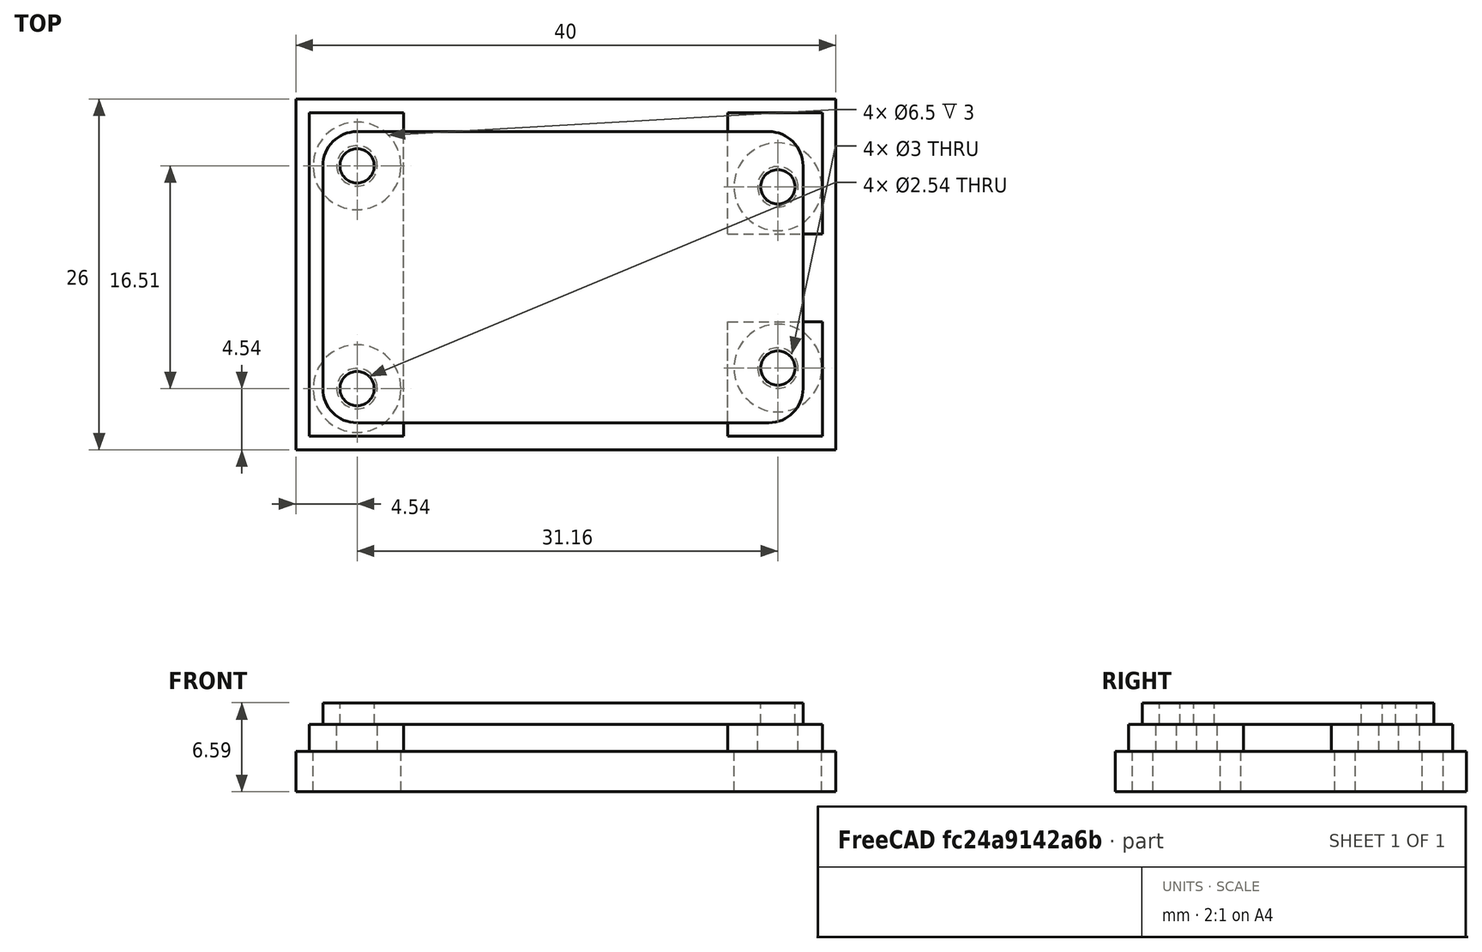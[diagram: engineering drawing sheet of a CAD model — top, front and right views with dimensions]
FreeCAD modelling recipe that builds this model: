
FCSTD DOCUMENT  (FreeCAD 0.19R)
Label: PowerRegulatorBase
License: All rights reserved
LicenseURL: http://en.wikipedia.org/wiki/All_rights_reserved
objects: Part::Cylinder×12, Part::MultiFuse×6, Part::Box×5, Part::Cut×2, Part::Fillet×1
note: 26 computed .brp shape members not serialized (recipe doc carries the construction recipe); baked Part::Feature solids carry a one-line shape summary decoded from their .brp

FEATURE [Part::Box] Box  label="Cube"
  AttacherType = Attacher::AttachEngine3D
  Height = 1.5875
  Length = 35.56
  Width = 21.59
FEATURE [Part::Fillet] Fillet
  Base = -> Box
  Edges = 4 edges r=2.54: [Edge1,Edge3,Edge5,Edge7]
FEATURE [Part::Cylinder] Cylinder
  Angle = 360
  AttacherType = Attacher::AttachEngine3D
  Height = 1.6
  Placement = pos=(2.54,2.54,0) rot=(0,0,1;0rad)
  Radius = 1.27
FEATURE [Part::Cylinder] Cylinder001
  Angle = 360
  AttacherType = Attacher::AttachEngine3D
  Height = 1.6
  Placement = pos=(2.54,19.05,0) rot=(0,0,1;0rad)
  Radius = 1.27
FEATURE [Part::Cylinder] Cylinder002
  Angle = 360
  AttacherType = Attacher::AttachEngine3D
  Height = 1.6
  Placement = pos=(33.7,4.064,0) rot=(0,0,1;0rad)
  Radius = 1.27
FEATURE [Part::Cylinder] Cylinder003
  Angle = 360
  AttacherType = Attacher::AttachEngine3D
  Height = 1.6
  Placement = pos=(33.7,17.5,0) rot=(0,0,1;0rad)
  Radius = 1.27
FEATURE [Part::MultiFuse] Fusion  label="Mounting Holes"
  Shapes = -> [Cylinder,Cylinder001,Cylinder003,Cylinder002]
FEATURE [Part::Cut] Cut  label="Regulator Object"
  Base = -> Fillet
  Placement = pos=(1,1,5) rot=(0,0,1;0rad)
  Tool = -> Fusion
FEATURE [Part::Box] Box001  label="Main Plate"
  AttacherType = Attacher::AttachEngine3D
  Height = 3
  Length = 40
  Placement = pos=(-1,-1,0) rot=(0,0,1;0rad)
  Width = 26
FEATURE [Part::Cylinder] Cylinder004
  Angle = 360
  AttacherType = Attacher::AttachEngine3D
  Height = 5
  Placement = pos=(2.54,19.05,0) rot=(0,0,1;0rad)
  Radius = 1.5
FEATURE [Part::Cylinder] Cylinder005
  Angle = 360
  AttacherType = Attacher::AttachEngine3D
  Height = 5
  Placement = pos=(2.54,2.54,0) rot=(0,0,1;0rad)
  Radius = 1.5
FEATURE [Part::Cylinder] Cylinder006
  Angle = 360
  AttacherType = Attacher::AttachEngine3D
  Height = 5
  Placement = pos=(33.7,17.5,0) rot=(0,0,1;0rad)
  Radius = 1.5
FEATURE [Part::Cylinder] Cylinder007
  Angle = 360
  AttacherType = Attacher::AttachEngine3D
  Height = 5
  Placement = pos=(33.7,4.064,0) rot=(0,0,1;0rad)
  Radius = 1.5
FEATURE [Part::MultiFuse] Fusion001  label="Screw Holes"
  Placement = pos=(1,1,0) rot=(0,0,1;0rad)
  Shapes = -> [Cylinder005,Cylinder004,Cylinder006,Cylinder007]
FEATURE [Part::Box] Box002  label="Cube002"
  AttacherType = Attacher::AttachEngine3D
  Height = 2
  Length = 7
  Placement = pos=(0,0,3) rot=(0,0,1;0rad)
  Width = 24
FEATURE [Part::Box] Box003  label="Cube003"
  AttacherType = Attacher::AttachEngine3D
  Height = 2
  Length = 7
  Placement = pos=(31,15,3) rot=(0,0,1;0rad)
  Width = 9
FEATURE [Part::Box] Box004  label="Cube004"
  AttacherType = Attacher::AttachEngine3D
  Height = 2
  Length = 7
  Placement = pos=(31,0,3) rot=(0,0,1;0rad)
  Width = 8.5
FEATURE [Part::Cylinder] Cylinder008
  Angle = 360
  AttacherType = Attacher::AttachEngine3D
  Height = 3
  Placement = pos=(3.54,20.05,0) rot=(0,0,1;0rad)
  Radius = 3.25
FEATURE [Part::Cylinder] Cylinder009
  Angle = 360
  AttacherType = Attacher::AttachEngine3D
  Height = 3
  Placement = pos=(3.54,3.54,0) rot=(0,0,1;0rad)
  Radius = 3.25
FEATURE [Part::MultiFuse] Fusion002  label="Standoff Blocks"
  Shapes = -> [Box002,Box003,Box004]
FEATURE [Part::Cylinder] Cylinder010
  Angle = 360
  AttacherType = Attacher::AttachEngine3D
  Height = 3
  Placement = pos=(34.7,18.5,0) rot=(0,0,1;0rad)
  Radius = 3.25
FEATURE [Part::Cylinder] Cylinder011
  Angle = 360
  AttacherType = Attacher::AttachEngine3D
  Height = 3
  Placement = pos=(34.7,5.06,0) rot=(0,0,1;0rad)
  Radius = 3.25
FEATURE [Part::MultiFuse] Fusion003  label="Washer Bolt Holes"
  Shapes = -> [Cylinder008,Cylinder009,Cylinder010,Cylinder011]
FEATURE [Part::MultiFuse] Fusion004  label="Complete Blackplate Holes"
  Shapes = -> [Fusion001,Fusion003]
FEATURE [Part::MultiFuse] Fusion005
  Shapes = -> [Box001,Fusion002]
FEATURE [Part::Cut] Cut001  label="Regulator Base"
  Base = -> Fusion005
  Tool = -> Fusion004
